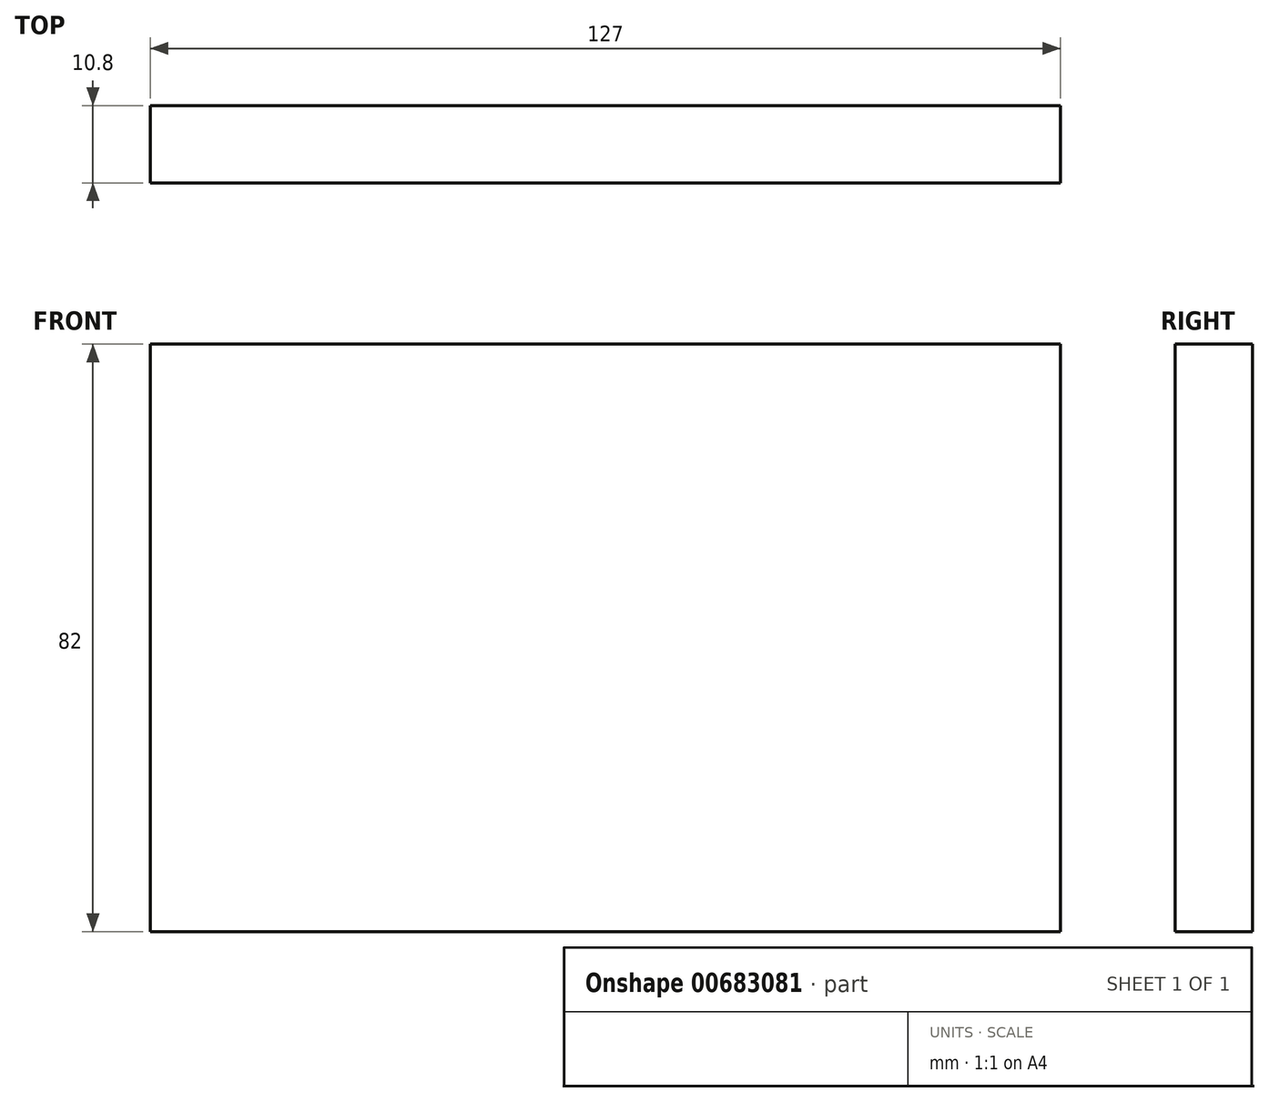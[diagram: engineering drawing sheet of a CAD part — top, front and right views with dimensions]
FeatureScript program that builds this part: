
annotation { "Feature Type Name" : "Feature", "Feature Type Description" : "" }
export const myFeature = defineFeature(function(context is Context, id is Id, definition is map)
    precondition{}
    {
        {
            var Q0;
            Q0=qCreatedBy(makeId("Top.planeOp"),FACE);
            var sketch = newSketch(context, id + "F0", { "sketchPlane" : qUnion([Q0])});
            skLineSegment(sketch, "E0.bottom", {"start": v(60.3, -5.4) * mm, "end": v(-66.7, -5.4) * mm});
            skLineSegment(sketch, "E0.top", {"start": v(60.3, 5.4) * mm, "end": v(-66.7, 5.4) * mm});
            skLineSegment(sketch, "E0.left", {"start": v(60.3, -5.4) * mm, "end": v(60.3, 5.4) * mm});
            skLineSegment(sketch, "E0.right", {"start": v(-66.7, -5.4) * mm, "end": v(-66.7, 5.4) * mm});
            skPoint(sketch, "E0.middle", {"position": v(-3.2, 0) * mm});
            skSolve(sketch);
        }
        {
            var Q0;
            Q0=makeQuery(id+"F0.imprint","IMPRINT",FACE,{"disambiguationData":[TD([[makeQuery(id+"F0.imprint","IMPRINT",EDGE,{"derivedFrom":sQuery(id+"F0.wireOp",EDGE,"E0.bottom")}),-1.0]])]});
            extrude(context, id + "F1", {"entities" : qUnion([Q0]), "depth" : 82 * mm, "offsetDistance" : 25 * mm});
        }
    });
